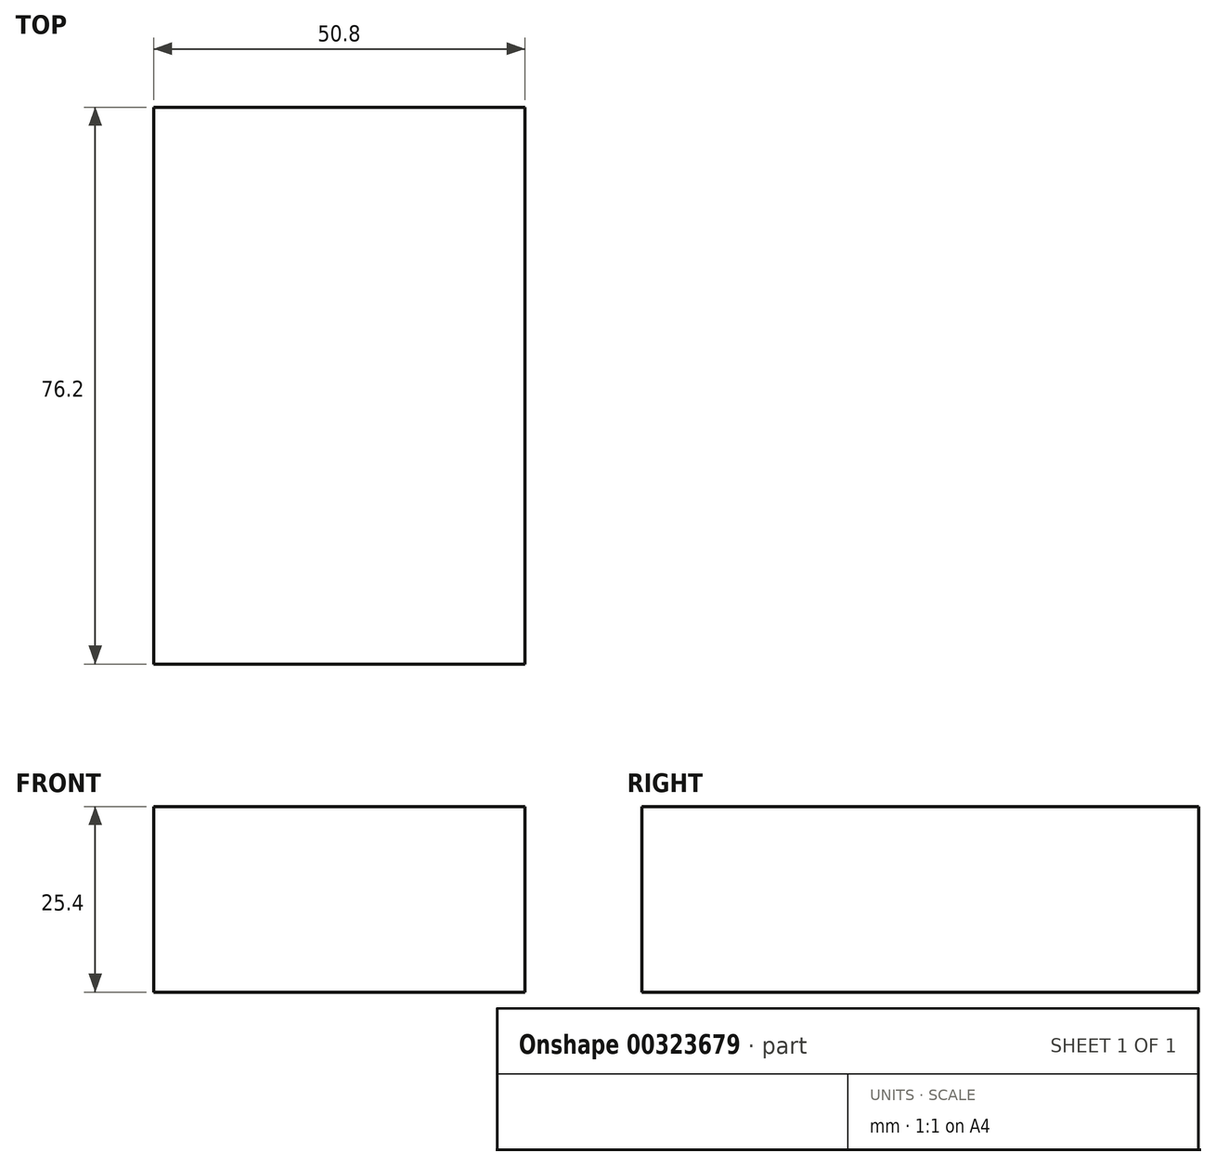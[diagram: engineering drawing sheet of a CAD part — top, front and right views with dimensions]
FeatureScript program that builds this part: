
annotation { "Feature Type Name" : "Feature", "Feature Type Description" : "" }
export const myFeature = defineFeature(function(context is Context, id is Id, definition is map)
    precondition{}
    {
        {
            var Q0;
            Q0=qCreatedBy(makeId("Front.planeOp"),FACE);
            var sketch = newSketch(context, id + "F0", { "sketchPlane" : qUnion([Q0])});
            skLineSegment(sketch, "E0.bottom", {"start": v(-39.6, 3.91) * mm, "end": v(11.2, 3.91) * mm});
            skLineSegment(sketch, "E0.top", {"start": v(-39.6, -21.49) * mm, "end": v(11.2, -21.49) * mm});
            skLineSegment(sketch, "E0.left", {"start": v(-39.6, 3.91) * mm, "end": v(-39.6, -21.49) * mm});
            skLineSegment(sketch, "E0.right", {"start": v(11.2, 3.91) * mm, "end": v(11.2, -21.49) * mm});
            skSolve(sketch);
        }
        {
            var Q0;
            Q0 = qSketchRegion(id + "F0", true);
            extrude(context, id + "F1", {"entities" : qUnion([Q0]), "depth" : 76.2 * mm});
        }
    });
